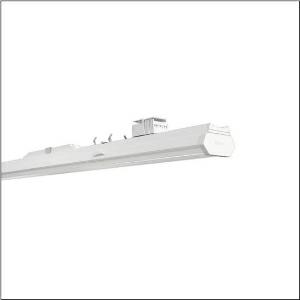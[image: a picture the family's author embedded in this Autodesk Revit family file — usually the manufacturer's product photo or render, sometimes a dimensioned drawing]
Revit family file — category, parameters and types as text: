
# Revit family: licross_11_protected_mo_51td1bdn49xgd
name_source: partatom
category: Lighting Fixtures
units: mm (PartAtom-declared; Revit-internal decimal feet)

## family parameters
Cut with Voids When Loaded = No
Host = Face
Light Source = No
Part Type = Normal
Room Calculation Point = No
Round Connector Dimension = Use Diameter
Shared = No

## types (1)
- --- (1 x LED, 1410 lm, 9.3 W, 4000K)
    Apparent Load = 9 VA
    CIE Flux Codes = 54 82 95 97 100
    Color Rendering = 80
    Color Temperature = 4000K
    Default Elevation = 1800 mm
    Description = Licross 11 Protected MO, luminaire insert, of sheet steel, galvanised, coil coated, white, length: 1.500mm, width: 90mm, height: 101mm, LED rated luminous flux: 9.370lm, light colour: 840, SDCM (Standard Deviation of Colour Matching)MacAdam ≤ 2 SDCM (initial), control gear: DALI 2 (for two DALI lines), with plug, 6-pole, with phase selection, mains connection: 220..240V, AC/DC, 0/50..60Hz, rated input power: 57W, internal wiring halogen-free, for central battery installations according to EN 60598-2-22, for emergency light function, without changeover relay, primary optical cover: cover, of PMMA, light emission: direct distribution, primary light characteristic: symmetric, protection rating (complete): IP54, insulation class (complete): insulation class I (protective earthing), certification: CE, ENEC, VDE, UKCA, protection symbol: D if used in an environment with non-conductive dust loads with corresponding accessories, impact resistance: IK06, permissible ambient temperature for indoor applications: -25..+35°C, standard: EN 60598-2-22, corresponds to IFS (International Featured Standards) requirements for safety and quality in the food industry, reducing of maximum allowable ambient temperature of 5°C with ceiling mounting, LABS conformity tested according to VDMA 24364:2018-05, The light source and the operating device comply with the requirements of the Ecodesign Regulation (EU) 2019/2020 and are replaceable in accordance with this regulation, packaging unit: 1 piece
    Height = 92 mm
    Lamp = 1 x LED
    Lamp Light Flux = 1410 lm
    Lamp Power = 9.3 W
    Lamp count = 1
    Length = 1500 mm
    Luminous efficacy = 152 lm/W
    Manufacturer = Siteco
    ModVariant = No
    Model = 51TD1BDN49XGD
    Mounting Place = Ceiling
    Mounting Type = Pendant
    Number of Poles = 1
    OnlyDefault = Yes
    Power Factor = 1
    Product Name = Licross 11 Protected MO
    Product group = luminaire insert | ceiling pendant
    ProductGroupID = 901
    Protection Class = Protection class I
    Protection Degree = IP 54
    RLX_Detail_Level = 1
    RLX_Emergency_Light_Flux = 0 lm
    RLX_Emergency_Type = 0
    RLX_Emergency_Type_DB = No
    RlxData = <blob elided: 25133 chars, md5=30b26554>
    Socket = socket
    Standby Power = 0 W
    System Light Flux = 1410 lm
    System Power = 9 W
    Type Comments = : DC mode (central or group accumulator) initial emergency light level
    Type Image = l_1256145.jpg
    URL = http://relux.com
    VarID = @adj_091661
    Voltage = 0 V
    Weight = 0.00 kg
    Width = 88 mm

## geometry (parser evidence)
native form markers: Blend x4, Sweep x10
no freeform markers — native parametric forms only
